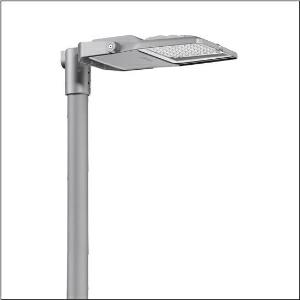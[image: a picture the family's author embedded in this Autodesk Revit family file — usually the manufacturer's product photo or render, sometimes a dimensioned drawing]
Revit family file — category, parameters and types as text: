
# Revit family: floodlight_fl_21_mini___pl52_5xa7776d2d3a_85e1
name_source: partatom
category: Lighting Fixtures
units: mm (PartAtom-declared; Revit-internal decimal feet)

## family parameters
Cut with Voids When Loaded = No
Host = Face
Light Source = No
Part Type = Normal
Room Calculation Point = No
Round Connector Dimension = Use Diameter
Shared = No

## types (1)
- --- (1 x LED, 17840 lm, 142.9 W, 3000K)
    Apparent Load = 143 VA
    CIE Flux Codes = 26 60 98 100 100
    Color Rendering = 70
    Color Temperature = 3000K
    Default Elevation = 1800 mm
    Description = Floodlight FL 21 mini, floodlight, primary light control with lens, of PMMA, primary optical cover: protective disc, of toughened safety glass, transparent, light distribution: PL52, light emission: direct distribution, installation type: surface-mounted, LED, High Power LED, rated luminous flux: 17.840lm, luminous efficacy: 125lm/W, light colour: 730, colour temperature: 3000K, control: flexible luminous flux parameterisation, time-dependent luminous flux control, constant luminous flux control, overheat protection, pre-setting: logarithmic dimming characteristic, with terminal, 6-pole, mains connection: 220..240V, AC, 50/60Hz, start of lifetime: 143W, end of service life: 151W, reduction: 63W, luminaire housing, of diecast aluminium, powder-coated, Siteco® metallic grey (DB 702S), corrosivity category C5 mid according to DIN EN ISO 12944, sealing non-destructively replaceable, please order mast flange separately, mast bracket, of steel, galvanised, powder-coated, Siteco® metallic grey (DB 702S), Smart Interface below and above, protection rating (complete): IP66, insulation class (complete): insulation class II (safety insulation), certification: CE, ENEC, VDE, protection symbol: D, impact resistance: IK08, permissible operating ambient temperature: -40..+40°C, permissible operating ambient temperature for outdoor applications: -40..+50°C, standard: DIN EN 12944, LABS conformity tested according to VDMA 24364:2018-05, packaging unit: 1 piece

Light Distribution: PL52
    Height = 70 mm
    Lamp = 1 x LED
    Lamp Light Flux = 17840 lm
    Lamp Power = 142.9 W
    Lamp count = 1
    Length = 485 mm
    Luminous efficacy = 125 lm/W
    Manufacturer = Siteco
    ModVariant = No
    Model = 5XA7776D2D3A
    Number of Poles = 1
    OnlyDefault = Yes
    Power Factor = 1
    Product Name = Floodlight FL 21 mini | PL52
    Product group = floodlight | pylon annexe
    ProductGroupID = 6200
    Protection Class = Protection class II
    Protection Degree = IP 66
    RLX_Detail_Level = 1
    RLX_Emergency_Light_Flux = 0 lm
    RLX_Emergency_Type = 0
    RLX_Emergency_Type_DB = No
    RlxData = <blob elided: 101549 chars, md5=c332d669>
    Socket = socket
    Standby Power = 0 W
    System Light Flux = 17840 lm
    System Power = 143 W
    Type Comments = factory setting: luminous flux: 100 % | dim-lin: 254 | 730 mA
    Type Image = l_1007125.jpg
    URL = http://relux.com
    VarID = @adj_133447
    Voltage = 0 V
    Weight = 0.00 kg
    Width = 337 mm

## geometry (parser evidence)
native form markers: Blend x4, Sweep x14
no freeform markers — native parametric forms only
